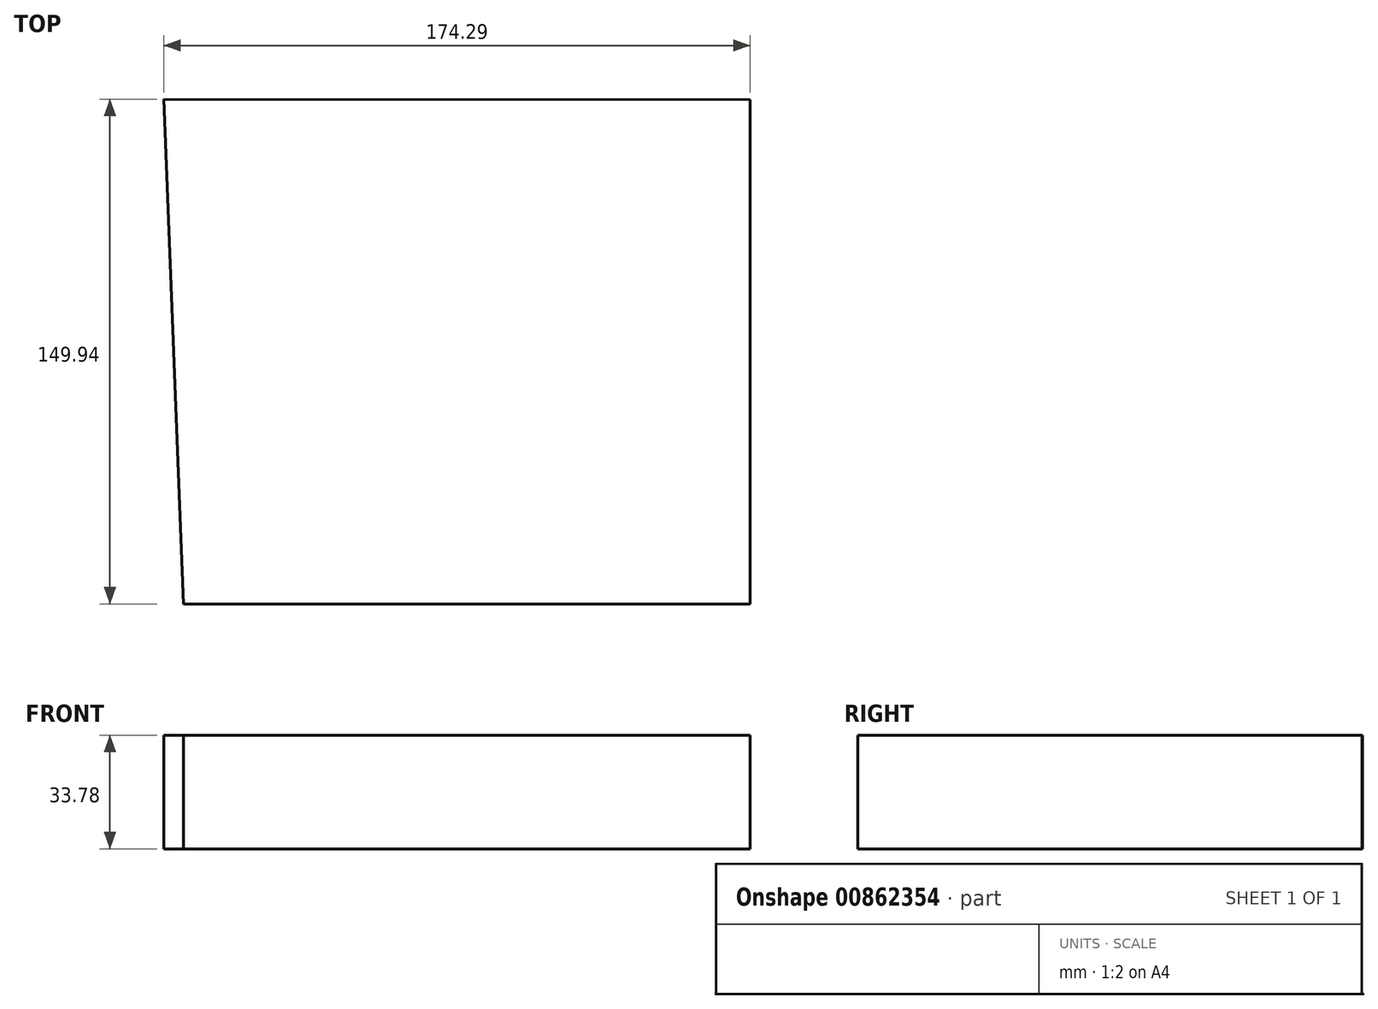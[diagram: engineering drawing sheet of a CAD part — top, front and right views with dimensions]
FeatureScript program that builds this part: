
annotation { "Feature Type Name" : "Feature", "Feature Type Description" : "" }
export const myFeature = defineFeature(function(context is Context, id is Id, definition is map)
    precondition{}
    {
        {
            var Q0;
            Q0=qCreatedBy(makeId("Top.planeOp"),FACE);
            var sketch = newSketch(context, id + "F0", { "sketchPlane" : qUnion([Q0])});
            skLineSegment(sketch, "E0", {"start": v(-105.95, 83.58) * mm, "end": v(-100.1, -66.36) * mm});
            skLineSegment(sketch, "E1", {"start": v(-100.1, -66.36) * mm, "end": v(68.34, -66.36) * mm});
            skLineSegment(sketch, "E2", {"start": v(68.34, -66.36) * mm, "end": v(68.34, 83.44) * mm});
            skLineSegment(sketch, "E3", {"start": v(68.34, 83.44) * mm, "end": v(-105.95, 83.58) * mm});
            skSolve(sketch);
        }
        {
            var Q0;
            Q0=makeQuery(id+"F0.imprint","IMPRINT",FACE,{"disambiguationData":[TD([[makeQuery(id+"F0.imprint","IMPRINT",EDGE,{"derivedFrom":sQuery(id+"F0.wireOp",EDGE,"E0")}),1.0]])]});
            extrude(context, id + "F1", {"entities" : qUnion([Q0]), "depth" : 33.78 * mm, "offsetDistance" : 25.4 * mm});
        }
    });
